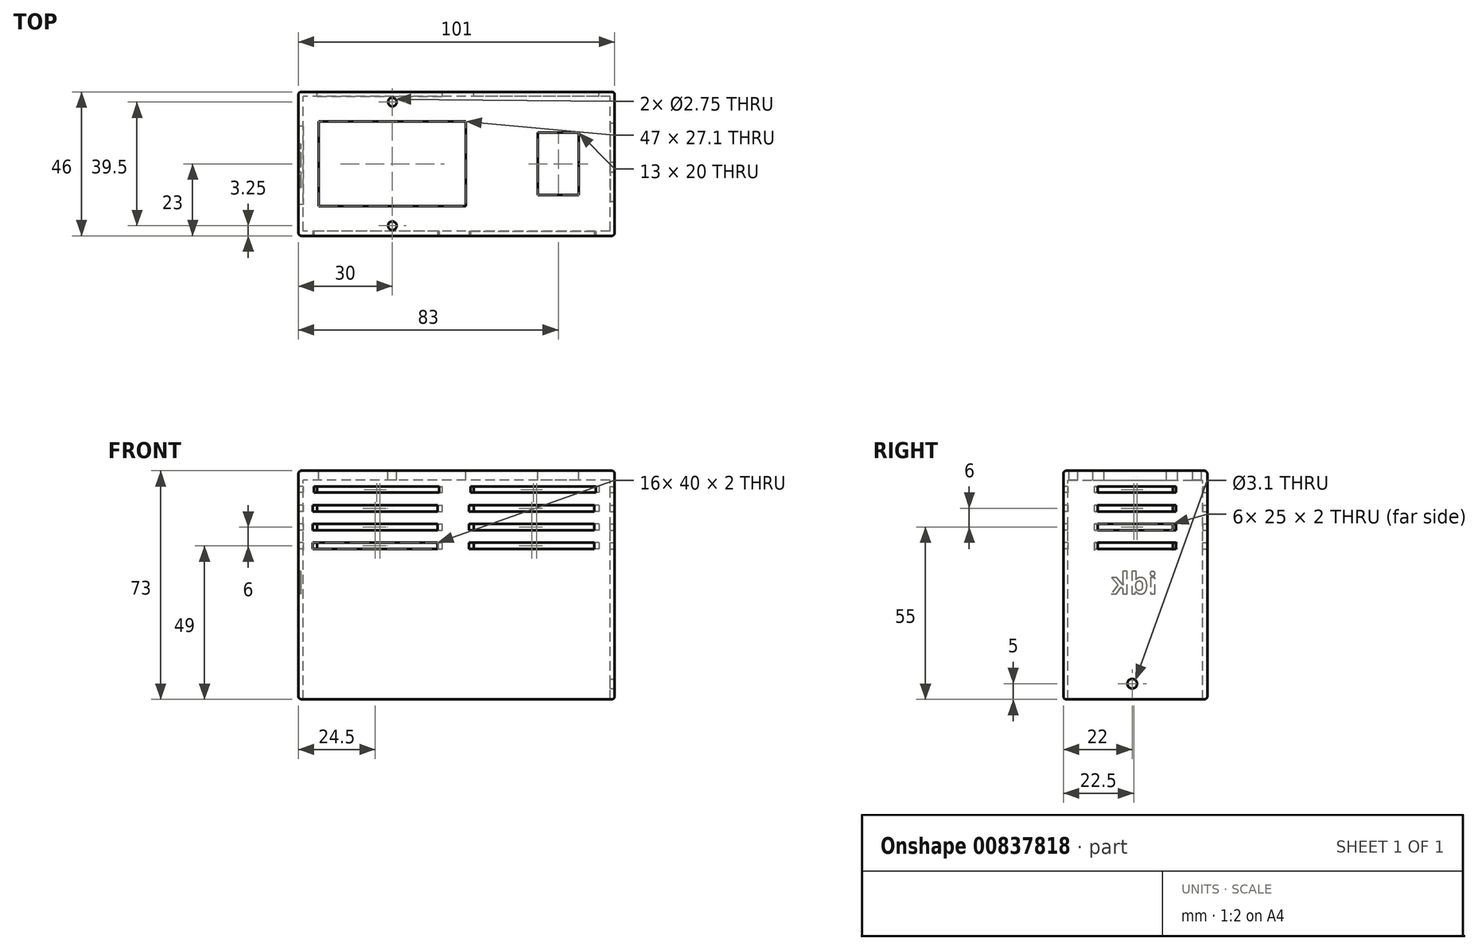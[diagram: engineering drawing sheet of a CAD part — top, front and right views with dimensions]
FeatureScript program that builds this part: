
annotation { "Feature Type Name" : "Feature", "Feature Type Description" : "" }
export const myFeature = defineFeature(function(context is Context, id is Id, definition is map)
    precondition{}
    {
        {
            var Q0;
            Q0=qCreatedBy(makeId("Top.planeOp"),FACE);
            var sketch = newSketch(context, id + "F0", { "sketchPlane" : qUnion([Q0])});
            skLineSegment(sketch, "E0.bottom", {"start": v(49, -21.5) * mm, "end": v(-49, -21.5) * mm});
            skLineSegment(sketch, "E0.top", {"start": v(49, 21.5) * mm, "end": v(-49, 21.5) * mm});
            skLineSegment(sketch, "E0.left", {"start": v(49, -21.5) * mm, "end": v(49, 21.5) * mm});
            skLineSegment(sketch, "E0.right", {"start": v(-49, -21.5) * mm, "end": v(-49, 21.5) * mm});
            skPoint(sketch, "E0.middle", {"position": v(0, 0) * mm});
            skLineSegment(sketch, "E1.bottom", {"start": v(50.5, -23) * mm, "end": v(-50.5, -23) * mm});
            skLineSegment(sketch, "E1.top", {"start": v(50.5, 23) * mm, "end": v(-50.5, 23) * mm});
            skLineSegment(sketch, "E1.left", {"start": v(50.5, -23) * mm, "end": v(50.5, 23) * mm});
            skLineSegment(sketch, "E1.right", {"start": v(-50.5, -23) * mm, "end": v(-50.5, 23) * mm});
            skLineSegment(sketch, "E2.bottom", {"start": v(3, -13.55) * mm, "end": v(-44, -13.55) * mm});
            skLineSegment(sketch, "E2.top", {"start": v(3, 13.55) * mm, "end": v(-44, 13.55) * mm});
            skLineSegment(sketch, "E2.left", {"start": v(3, -13.55) * mm, "end": v(3, 13.55) * mm});
            skLineSegment(sketch, "E2.right", {"start": v(-44, -13.55) * mm, "end": v(-44, 13.55) * mm});
            skPoint(sketch, "E2.middle", {"position": v(-20.5, 0) * mm});
            skLineSegment(sketch, "E3.bottom", {"start": v(39, -10) * mm, "end": v(26, -10) * mm});
            skLineSegment(sketch, "E3.top", {"start": v(39, 10) * mm, "end": v(26, 10) * mm});
            skLineSegment(sketch, "E3.left", {"start": v(39, -10) * mm, "end": v(39, 10) * mm});
            skLineSegment(sketch, "E3.right", {"start": v(26, -10) * mm, "end": v(26, 10) * mm});
            skPoint(sketch, "E3.middle", {"position": v(32.5, 0) * mm});
            skCircle(sketch, "E4", {"center": v(-20.5, -19.75) * mm, "radius": 1.38 * mm});
            skCircle(sketch, "E5", {"center": v(-20.5, 19.75) * mm, "radius": 1.38 * mm});
            skSolve(sketch);
        }
        {
            var Q0;
            Q0=makeQuery(id+"F0.imprint","IMPRINT",FACE,{"disambiguationData":[TD([[makeQuery(id+"F0.imprint","IMPRINT",EDGE,{"derivedFrom":sQuery(id+"F0.wireOp",EDGE,"E0.bottom")}),1.0]])]});
            extrude(context, id + "F1", {"entities" : qUnion([Q0]), "oppositeDirection" : true, "depth" : 73 * mm, "offsetDistance" : 25 * mm});
        }
        {
            var Q0;
            Q0=makeQuery(id+"F0.imprint","IMPRINT",FACE,{"disambiguationData":[TD([[makeQuery(id+"F0.imprint","IMPRINT",EDGE,{"derivedFrom":sQuery(id+"F0.wireOp",EDGE,"E0.bottom")}),-1.0]])]});
            extrude(context, id + "F2", {"entities" : qUnion([Q0]), "operationType" : NewBodyOperationType.ADD, "oppositeDirection" : true, "depth" : 3 * mm, "offsetDistance" : 25 * mm});
        }
        {
            var Q0;
            Q0=qCreatedBy(makeId("Right.planeOp"),FACE);
            cPlane(context, id + "F3", {"entities" : qUnion([Q0]), "cplaneType" : CPlaneType.OFFSET, "offset" : 49 * mm, "width" : 150 * mm, "height" : 150 * mm});
        }
        {
            var Q0;
            Q0=makeQuery(id+"F1.opExtrude","SWEPT_FACE",FACE,{"disambiguationData":[OSD([sQuery(id+"F0.wireOp",EDGE,"E1.left")])]});
            var sketch = newSketch(context, id + "F4", { "sketchPlane" : qUnion([Q0])});
            skCircle(sketch, "E6", {"center": v(-1, -68) * mm, "radius": 1.55 * mm});
            skSolve(sketch);
        }
        {
            var Q0;
            Q0=makeQuery(id+"F4.imprint","IMPRINT",FACE,{"disambiguationData":[TD([[makeQuery(id+"F4.imprint","IMPRINT",EDGE,{"derivedFrom":sQuery(id+"F4.wireOp",EDGE,"E6")}),1.0]])]});
            extrude(context, id + "F5", {"entities" : qUnion([Q0]), "operationType" : NewBodyOperationType.REMOVE, "oppositeDirection" : true, "depth" : 3 * mm, "offsetDistance" : 25 * mm});
        }
        {
            var Q0;
            Q0=makeQuery(id+"F1.opExtrude","CAP_EDGE",EDGE,{"disambiguationData":[OSD([sQuery(id+"F0.wireOp",EDGE,"E1.bottom")])],"isStart":false});
            var Q1;
            Q1=makeQuery(id+"F1.opExtrude","CAP_EDGE",EDGE,{"disambiguationData":[OSD([sQuery(id+"F0.wireOp",EDGE,"E1.left")])],"isStart":false});
            var Q2;
            Q2=makeQuery(id+"F1.opExtrude","CAP_EDGE",EDGE,{"disambiguationData":[OSD([sQuery(id+"F0.wireOp",EDGE,"E1.top")])],"isStart":false});
            var Q3;
            Q3=makeQuery(id+"F1.opExtrude","CAP_EDGE",EDGE,{"disambiguationData":[OSD([sQuery(id+"F0.wireOp",EDGE,"E1.right")])],"isStart":false});
            var Q4;
            Q4=makeQuery(id+"F1.opExtrude","SWEPT_EDGE",EDGE,{"disambiguationData":[OSD([sQuery(id+"F0.wireOp",EDGE,"E1.bottom"),sQuery(id+"F0.wireOp",EDGE,"E1.right")])]});
            var Q5;
            Q5=makeQuery(id+"F1.opExtrude","SWEPT_EDGE",EDGE,{"disambiguationData":[OSD([sQuery(id+"F0.wireOp",EDGE,"E1.top"),sQuery(id+"F0.wireOp",EDGE,"E1.right")])]});
            var Q6;
            Q6=makeQuery(id+"F1.opExtrude","SWEPT_EDGE",EDGE,{"disambiguationData":[OSD([sQuery(id+"F0.wireOp",EDGE,"E1.bottom"),sQuery(id+"F0.wireOp",EDGE,"E1.left")])]});
            var Q7;
            Q7=makeQuery(id+"F1.opExtrude","SWEPT_EDGE",EDGE,{"disambiguationData":[OSD([sQuery(id+"F0.wireOp",EDGE,"E1.top"),sQuery(id+"F0.wireOp",EDGE,"E1.left")])]});
            var Q8;
            Q8=makeQuery(id+"F1.opExtrude","CAP_EDGE",EDGE,{"disambiguationData":[OSD([sQuery(id+"F0.wireOp",EDGE,"E1.bottom")])],"isStart":true});
            var Q9;
            Q9=makeQuery(id+"F1.opExtrude","CAP_EDGE",EDGE,{"disambiguationData":[OSD([sQuery(id+"F0.wireOp",EDGE,"E1.left")])],"isStart":true});
            var Q10;
            Q10=makeQuery(id+"F1.opExtrude","CAP_EDGE",EDGE,{"disambiguationData":[OSD([sQuery(id+"F0.wireOp",EDGE,"E1.top")])],"isStart":true});
            var Q11;
            Q11=makeQuery(id+"F1.opExtrude","CAP_EDGE",EDGE,{"disambiguationData":[OSD([sQuery(id+"F0.wireOp",EDGE,"E1.right")])],"isStart":true});
            var Q12;
            Q12=makeQuery(id+"F5.boolean.opBoolean","COPY",EDGE,{"derivedFrom":makeQuery(id+"F5.opExtrude","CAP_EDGE",EDGE,{"disambiguationData":[OSD([sQuery(id+"F4.wireOp",EDGE,"E6")])],"isStart":true})});
            fillet(context, id + "F6", {"entities" : qUnion([Q0, Q1, Q2, Q3, Q4, Q5, Q6, Q7, Q8, Q9, Q10, Q11, Q12]), "radius" : 1 * mm, "tangentPropagation" : true, "allowEdgeOverflow" : false});
        }
        {
            var Q0;
            Q0=makeQuery(id+"F1.opExtrude","SWEPT_FACE",FACE,{"disambiguationData":[OSD([sQuery(id+"F0.wireOp",EDGE,"E1.bottom")])]});
            var sketch = newSketch(context, id + "F7", { "sketchPlane" : qUnion([Q0])});
            skLineSegment(sketch, "E7.bottom", {"start": v(44.5, -7) * mm, "end": v(4.5, -7) * mm});
            skLineSegment(sketch, "E7.top", {"start": v(44.5, -5) * mm, "end": v(4.5, -5) * mm});
            skLineSegment(sketch, "E7.left", {"start": v(44.5, -7) * mm, "end": v(44.5, -5) * mm});
            skLineSegment(sketch, "E7.right", {"start": v(4.5, -7) * mm, "end": v(4.5, -5) * mm});
            skPoint(sketch, "E7.middle", {"position": v(24.5, -6) * mm});
            skLineSegment(sketch, "E8.bottom", {"start": v(-45.5, -5) * mm, "end": v(-5.5, -5) * mm});
            skLineSegment(sketch, "E8.top", {"start": v(-45.5, -7) * mm, "end": v(-5.5, -7) * mm});
            skLineSegment(sketch, "E8.left", {"start": v(-45.5, -5) * mm, "end": v(-45.5, -7) * mm});
            skLineSegment(sketch, "E8.right", {"start": v(-5.5, -5) * mm, "end": v(-5.5, -7) * mm});
            skPoint(sketch, "E8.middle", {"position": v(-25.5, -6) * mm});
            skLineSegment(sketch, "E9.bottom", {"start": v(44, -13) * mm, "end": v(4, -13) * mm});
            skLineSegment(sketch, "E9.top", {"start": v(44, -11) * mm, "end": v(4, -11) * mm});
            skLineSegment(sketch, "E9.left", {"start": v(44, -13) * mm, "end": v(44, -11) * mm});
            skLineSegment(sketch, "E9.right", {"start": v(4, -13) * mm, "end": v(4, -11) * mm});
            skPoint(sketch, "E9.middle", {"position": v(24, -12) * mm});
            skLineSegment(sketch, "E10.bottom", {"start": v(-46, -11) * mm, "end": v(-6, -11) * mm});
            skLineSegment(sketch, "E10.top", {"start": v(-46, -13) * mm, "end": v(-6, -13) * mm});
            skLineSegment(sketch, "E10.left", {"start": v(-46, -11) * mm, "end": v(-46, -13) * mm});
            skLineSegment(sketch, "E10.right", {"start": v(-6, -11) * mm, "end": v(-6, -13) * mm});
            skPoint(sketch, "E10.middle", {"position": v(-26, -12) * mm});
            skLineSegment(sketch, "E11.bottom", {"start": v(44, -19) * mm, "end": v(4, -19) * mm});
            skLineSegment(sketch, "E11.top", {"start": v(44, -17) * mm, "end": v(4, -17) * mm});
            skLineSegment(sketch, "E11.left", {"start": v(44, -19) * mm, "end": v(44, -17) * mm});
            skLineSegment(sketch, "E11.right", {"start": v(4, -19) * mm, "end": v(4, -17) * mm});
            skPoint(sketch, "E11.middle", {"position": v(24, -18) * mm});
            skLineSegment(sketch, "E12.bottom", {"start": v(-46, -17) * mm, "end": v(-6, -17) * mm});
            skLineSegment(sketch, "E12.top", {"start": v(-46, -19) * mm, "end": v(-6, -19) * mm});
            skLineSegment(sketch, "E12.left", {"start": v(-46, -17) * mm, "end": v(-46, -19) * mm});
            skLineSegment(sketch, "E12.right", {"start": v(-6, -17) * mm, "end": v(-6, -19) * mm});
            skPoint(sketch, "E12.middle", {"position": v(-26, -18) * mm});
            skLineSegment(sketch, "E13.bottom", {"start": v(44, -25) * mm, "end": v(4, -25) * mm});
            skLineSegment(sketch, "E13.top", {"start": v(44, -23) * mm, "end": v(4, -23) * mm});
            skLineSegment(sketch, "E13.left", {"start": v(44, -25) * mm, "end": v(44, -23) * mm});
            skLineSegment(sketch, "E13.right", {"start": v(4, -25) * mm, "end": v(4, -23) * mm});
            skPoint(sketch, "E13.middle", {"position": v(24, -24) * mm});
            skLineSegment(sketch, "E14.bottom", {"start": v(-46, -23) * mm, "end": v(-6, -23) * mm});
            skLineSegment(sketch, "E14.top", {"start": v(-46, -25) * mm, "end": v(-6, -25) * mm});
            skLineSegment(sketch, "E14.left", {"start": v(-46, -23) * mm, "end": v(-46, -25) * mm});
            skLineSegment(sketch, "E14.right", {"start": v(-6, -23) * mm, "end": v(-6, -25) * mm});
            skPoint(sketch, "E14.middle", {"position": v(-26, -24) * mm});
            skSolve(sketch);
        }
        {
            var Q0;
            Q0=makeQuery(id+"F1.opExtrude","SWEPT_FACE",FACE,{"disambiguationData":[OSD([sQuery(id+"F0.wireOp",EDGE,"E1.top")])]});
            var sketch = newSketch(context, id + "F8", { "sketchPlane" : qUnion([Q0])});
            skLineSegment(sketch, "E15.bottom", {"start": v(44.5, -7) * mm, "end": v(4.5, -7) * mm});
            skLineSegment(sketch, "E15.top", {"start": v(44.5, -5) * mm, "end": v(4.5, -5) * mm});
            skLineSegment(sketch, "E15.left", {"start": v(44.5, -7) * mm, "end": v(44.5, -5) * mm});
            skLineSegment(sketch, "E15.right", {"start": v(4.5, -7) * mm, "end": v(4.5, -5) * mm});
            skPoint(sketch, "E15.middle", {"position": v(24.5, -6) * mm});
            skLineSegment(sketch, "E16.bottom", {"start": v(-45.5, -5) * mm, "end": v(-5.5, -5) * mm});
            skLineSegment(sketch, "E16.top", {"start": v(-45.5, -7) * mm, "end": v(-5.5, -7) * mm});
            skLineSegment(sketch, "E16.left", {"start": v(-45.5, -5) * mm, "end": v(-45.5, -7) * mm});
            skLineSegment(sketch, "E16.right", {"start": v(-5.5, -5) * mm, "end": v(-5.5, -7) * mm});
            skPoint(sketch, "E16.middle", {"position": v(-25.5, -6) * mm});
            skLineSegment(sketch, "E17.bottom", {"start": v(44.5, -13) * mm, "end": v(4.5, -13) * mm});
            skLineSegment(sketch, "E17.top", {"start": v(44.5, -11) * mm, "end": v(4.5, -11) * mm});
            skLineSegment(sketch, "E17.left", {"start": v(44.5, -13) * mm, "end": v(44.5, -11) * mm});
            skLineSegment(sketch, "E17.right", {"start": v(4.5, -13) * mm, "end": v(4.5, -11) * mm});
            skPoint(sketch, "E17.middle", {"position": v(24.5, -12) * mm});
            skLineSegment(sketch, "E18.bottom", {"start": v(-45.5, -11) * mm, "end": v(-5.5, -11) * mm});
            skLineSegment(sketch, "E18.top", {"start": v(-45.5, -13) * mm, "end": v(-5.5, -13) * mm});
            skLineSegment(sketch, "E18.left", {"start": v(-45.5, -11) * mm, "end": v(-45.5, -13) * mm});
            skLineSegment(sketch, "E18.right", {"start": v(-5.5, -11) * mm, "end": v(-5.5, -13) * mm});
            skPoint(sketch, "E18.middle", {"position": v(-25.5, -12) * mm});
            skLineSegment(sketch, "E19.bottom", {"start": v(44.5, -19) * mm, "end": v(4.5, -19) * mm});
            skLineSegment(sketch, "E19.top", {"start": v(44.5, -17) * mm, "end": v(4.5, -17) * mm});
            skLineSegment(sketch, "E19.left", {"start": v(44.5, -19) * mm, "end": v(44.5, -17) * mm});
            skLineSegment(sketch, "E19.right", {"start": v(4.5, -19) * mm, "end": v(4.5, -17) * mm});
            skPoint(sketch, "E19.middle", {"position": v(24.5, -18) * mm});
            skLineSegment(sketch, "E20.bottom", {"start": v(-45.5, -17) * mm, "end": v(-5.5, -17) * mm});
            skLineSegment(sketch, "E20.top", {"start": v(-45.5, -19) * mm, "end": v(-5.5, -19) * mm});
            skLineSegment(sketch, "E20.left", {"start": v(-45.5, -17) * mm, "end": v(-45.5, -19) * mm});
            skLineSegment(sketch, "E20.right", {"start": v(-5.5, -17) * mm, "end": v(-5.5, -19) * mm});
            skPoint(sketch, "E20.middle", {"position": v(-25.5, -18) * mm});
            skLineSegment(sketch, "E21.bottom", {"start": v(44.5, -25) * mm, "end": v(4.5, -25) * mm});
            skLineSegment(sketch, "E21.top", {"start": v(44.5, -23) * mm, "end": v(4.5, -23) * mm});
            skLineSegment(sketch, "E21.left", {"start": v(44.5, -25) * mm, "end": v(44.5, -23) * mm});
            skLineSegment(sketch, "E21.right", {"start": v(4.5, -25) * mm, "end": v(4.5, -23) * mm});
            skPoint(sketch, "E21.middle", {"position": v(24.5, -24) * mm});
            skLineSegment(sketch, "E22.bottom", {"start": v(-45.5, -23) * mm, "end": v(-5.5, -23) * mm});
            skLineSegment(sketch, "E22.top", {"start": v(-45.5, -25) * mm, "end": v(-5.5, -25) * mm});
            skLineSegment(sketch, "E22.left", {"start": v(-45.5, -23) * mm, "end": v(-45.5, -25) * mm});
            skLineSegment(sketch, "E22.right", {"start": v(-5.5, -23) * mm, "end": v(-5.5, -25) * mm});
            skPoint(sketch, "E22.middle", {"position": v(-25.5, -24) * mm});
            skSolve(sketch);
        }
        {
            var Q0;
            Q0 = qSketchRegion(id + "F8", true);
            extrude(context, id + "F9", {"entities" : qUnion([Q0]), "operationType" : NewBodyOperationType.REMOVE, "oppositeDirection" : true, "depth" : 3 * mm, "offsetDistance" : 25 * mm});
        }
        {
            var Q0;
            Q0 = qSketchRegion(id + "F7", true);
            extrude(context, id + "F10", {"entities" : qUnion([Q0]), "operationType" : NewBodyOperationType.REMOVE, "oppositeDirection" : true, "depth" : 3 * mm, "offsetDistance" : 25 * mm});
        }
        {
            var Q0;
            Q0=makeQuery(id+"F1.opExtrude","SWEPT_FACE",FACE,{"disambiguationData":[OSD([sQuery(id+"F0.wireOp",EDGE,"E1.left")])]});
            var sketch = newSketch(context, id + "F11", { "sketchPlane" : qUnion([Q0])});
            skLineSegment(sketch, "E23.bottom", {"start": v(13, -7) * mm, "end": v(-12, -7) * mm});
            skLineSegment(sketch, "E23.top", {"start": v(13, -5) * mm, "end": v(-12, -5) * mm});
            skLineSegment(sketch, "E23.left", {"start": v(13, -7) * mm, "end": v(13, -5) * mm});
            skLineSegment(sketch, "E23.right", {"start": v(-12, -7) * mm, "end": v(-12, -5) * mm});
            skPoint(sketch, "E23.middle", {"position": v(0.5, -6) * mm});
            skLineSegment(sketch, "E24.bottom", {"start": v(13, -13) * mm, "end": v(-12, -13) * mm});
            skLineSegment(sketch, "E24.top", {"start": v(13, -11) * mm, "end": v(-12, -11) * mm});
            skLineSegment(sketch, "E24.left", {"start": v(13, -13) * mm, "end": v(13, -11) * mm});
            skLineSegment(sketch, "E24.right", {"start": v(-12, -13) * mm, "end": v(-12, -11) * mm});
            skPoint(sketch, "E24.middle", {"position": v(0.5, -12) * mm});
            skLineSegment(sketch, "E25.bottom", {"start": v(13, -19) * mm, "end": v(-12, -19) * mm});
            skLineSegment(sketch, "E25.top", {"start": v(13, -17) * mm, "end": v(-12, -17) * mm});
            skLineSegment(sketch, "E25.left", {"start": v(13, -19) * mm, "end": v(13, -17) * mm});
            skLineSegment(sketch, "E25.right", {"start": v(-12, -19) * mm, "end": v(-12, -17) * mm});
            skPoint(sketch, "E25.middle", {"position": v(0.5, -18) * mm});
            skLineSegment(sketch, "E26.bottom", {"start": v(13, -25) * mm, "end": v(-12, -25) * mm});
            skLineSegment(sketch, "E26.top", {"start": v(13, -23) * mm, "end": v(-12, -23) * mm});
            skLineSegment(sketch, "E26.left", {"start": v(13, -25) * mm, "end": v(13, -23) * mm});
            skLineSegment(sketch, "E26.right", {"start": v(-12, -25) * mm, "end": v(-12, -23) * mm});
            skPoint(sketch, "E26.middle", {"position": v(0.5, -24) * mm});
            skSolve(sketch);
        }
        {
            var Q0;
            Q0 = qSketchRegion(id + "F11", true);
            extrude(context, id + "F12", {"entities" : qUnion([Q0]), "operationType" : NewBodyOperationType.REMOVE, "oppositeDirection" : true, "depth" : 3 * mm, "offsetDistance" : 25 * mm});
        }
        {
            var Q0;
            Q0=makeQuery(id+"F1.opExtrude","SWEPT_FACE",FACE,{"disambiguationData":[OSD([sQuery(id+"F0.wireOp",EDGE,"E1.right")])]});
            var sketch = newSketch(context, id + "F13", { "sketchPlane" : qUnion([Q0])});
            skLineSegment(sketch, "E27.bottom", {"start": v(13, -7) * mm, "end": v(-12, -7) * mm});
            skLineSegment(sketch, "E27.top", {"start": v(13, -5) * mm, "end": v(-12, -5) * mm});
            skLineSegment(sketch, "E27.left", {"start": v(13, -7) * mm, "end": v(13, -5) * mm});
            skLineSegment(sketch, "E27.right", {"start": v(-12, -7) * mm, "end": v(-12, -5) * mm});
            skPoint(sketch, "E27.middle", {"position": v(0.5, -6) * mm});
            skLineSegment(sketch, "E28.bottom", {"start": v(13, -13) * mm, "end": v(-12, -13) * mm});
            skLineSegment(sketch, "E28.top", {"start": v(13, -11) * mm, "end": v(-12, -11) * mm});
            skLineSegment(sketch, "E28.left", {"start": v(13, -13) * mm, "end": v(13, -11) * mm});
            skLineSegment(sketch, "E28.right", {"start": v(-12, -13) * mm, "end": v(-12, -11) * mm});
            skPoint(sketch, "E28.middle", {"position": v(0.5, -12) * mm});
            skLineSegment(sketch, "E29.bottom", {"start": v(13, -19) * mm, "end": v(-12, -19) * mm});
            skLineSegment(sketch, "E29.top", {"start": v(13, -17) * mm, "end": v(-12, -17) * mm});
            skLineSegment(sketch, "E29.left", {"start": v(13, -19) * mm, "end": v(13, -17) * mm});
            skLineSegment(sketch, "E29.right", {"start": v(-12, -19) * mm, "end": v(-12, -17) * mm});
            skPoint(sketch, "E29.middle", {"position": v(0.5, -18) * mm});
            skLineSegment(sketch, "E30.bottom", {"start": v(13, -25) * mm, "end": v(-12, -25) * mm});
            skLineSegment(sketch, "E30.top", {"start": v(13, -23) * mm, "end": v(-12, -23) * mm});
            skLineSegment(sketch, "E30.left", {"start": v(13, -25) * mm, "end": v(13, -23) * mm});
            skLineSegment(sketch, "E30.right", {"start": v(-12, -25) * mm, "end": v(-12, -23) * mm});
            skPoint(sketch, "E30.middle", {"position": v(0.5, -24) * mm});
            skSolve(sketch);
        }
        {
            var Q0;
            Q0 = qSketchRegion(id + "F13", true);
            extrude(context, id + "F14", {"entities" : qUnion([Q0]), "operationType" : NewBodyOperationType.REMOVE, "oppositeDirection" : true, "depth" : 3 * mm, "offsetDistance" : 25 * mm});
        }
        {
            var Q0;
            Q0=makeQuery(id+"F10.boolean.opBoolean","COPY",EDGE,{"derivedFrom":makeQuery(id+"F10.opExtrude","CAP_EDGE",EDGE,{"disambiguationData":[OSD([sQuery(id+"F7.wireOp",EDGE,"E13.left")])],"isStart":true})});
            var Q1;
            Q1=makeQuery(id+"F10.boolean.opBoolean","COPY",EDGE,{"derivedFrom":makeQuery(id+"F10.opExtrude","CAP_EDGE",EDGE,{"disambiguationData":[OSD([sQuery(id+"F7.wireOp",EDGE,"E13.bottom")])],"isStart":true})});
            var Q2;
            Q2=makeQuery(id+"F10.boolean.opBoolean","COPY",EDGE,{"derivedFrom":makeQuery(id+"F10.opExtrude","CAP_EDGE",EDGE,{"disambiguationData":[OSD([sQuery(id+"F7.wireOp",EDGE,"E13.top")])],"isStart":true})});
            var Q3;
            Q3=makeQuery(id+"F10.boolean.opBoolean","COPY",EDGE,{"derivedFrom":makeQuery(id+"F10.opExtrude","CAP_EDGE",EDGE,{"disambiguationData":[OSD([sQuery(id+"F7.wireOp",EDGE,"E13.right")])],"isStart":true})});
            var Q4;
            Q4=makeQuery(id+"F10.boolean.opBoolean","COPY",EDGE,{"derivedFrom":makeQuery(id+"F10.opExtrude","CAP_EDGE",EDGE,{"disambiguationData":[OSD([sQuery(id+"F7.wireOp",EDGE,"E11.bottom")])],"isStart":true})});
            var Q5;
            Q5=makeQuery(id+"F10.boolean.opBoolean","COPY",EDGE,{"derivedFrom":makeQuery(id+"F10.opExtrude","CAP_EDGE",EDGE,{"disambiguationData":[OSD([sQuery(id+"F7.wireOp",EDGE,"E11.left")])],"isStart":true})});
            var Q6;
            Q6=makeQuery(id+"F10.boolean.opBoolean","COPY",EDGE,{"derivedFrom":makeQuery(id+"F10.opExtrude","CAP_EDGE",EDGE,{"disambiguationData":[OSD([sQuery(id+"F7.wireOp",EDGE,"E11.top")])],"isStart":true})});
            var Q7;
            Q7=makeQuery(id+"F10.boolean.opBoolean","COPY",EDGE,{"derivedFrom":makeQuery(id+"F10.opExtrude","CAP_EDGE",EDGE,{"disambiguationData":[OSD([sQuery(id+"F7.wireOp",EDGE,"E11.right")])],"isStart":true})});
            var Q8;
            Q8=makeQuery(id+"F10.boolean.opBoolean","COPY",EDGE,{"derivedFrom":makeQuery(id+"F10.opExtrude","CAP_EDGE",EDGE,{"disambiguationData":[OSD([sQuery(id+"F7.wireOp",EDGE,"E9.right")])],"isStart":true})});
            var Q9;
            Q9=makeQuery(id+"F10.boolean.opBoolean","COPY",EDGE,{"derivedFrom":makeQuery(id+"F10.opExtrude","CAP_EDGE",EDGE,{"disambiguationData":[OSD([sQuery(id+"F7.wireOp",EDGE,"E9.bottom")])],"isStart":true})});
            var Q10;
            Q10=makeQuery(id+"F10.boolean.opBoolean","COPY",EDGE,{"derivedFrom":makeQuery(id+"F10.opExtrude","CAP_EDGE",EDGE,{"disambiguationData":[OSD([sQuery(id+"F7.wireOp",EDGE,"E9.left")])],"isStart":true})});
            var Q11;
            Q11=makeQuery(id+"F10.boolean.opBoolean","COPY",EDGE,{"derivedFrom":makeQuery(id+"F10.opExtrude","CAP_EDGE",EDGE,{"disambiguationData":[OSD([sQuery(id+"F7.wireOp",EDGE,"E9.top")])],"isStart":true})});
            var Q12;
            Q12=makeQuery(id+"F10.boolean.opBoolean","COPY",EDGE,{"derivedFrom":makeQuery(id+"F10.opExtrude","CAP_EDGE",EDGE,{"disambiguationData":[OSD([sQuery(id+"F7.wireOp",EDGE,"E7.bottom")])],"isStart":true})});
            var Q13;
            Q13=makeQuery(id+"F10.boolean.opBoolean","COPY",EDGE,{"derivedFrom":makeQuery(id+"F10.opExtrude","CAP_EDGE",EDGE,{"disambiguationData":[OSD([sQuery(id+"F7.wireOp",EDGE,"E7.left")])],"isStart":true})});
            var Q14;
            Q14=makeQuery(id+"F10.boolean.opBoolean","COPY",EDGE,{"derivedFrom":makeQuery(id+"F10.opExtrude","CAP_EDGE",EDGE,{"disambiguationData":[OSD([sQuery(id+"F7.wireOp",EDGE,"E7.top")])],"isStart":true})});
            var Q15;
            Q15=makeQuery(id+"F10.boolean.opBoolean","COPY",EDGE,{"derivedFrom":makeQuery(id+"F10.opExtrude","CAP_EDGE",EDGE,{"disambiguationData":[OSD([sQuery(id+"F7.wireOp",EDGE,"E7.right")])],"isStart":true})});
            var Q16;
            Q16=makeQuery(id+"F10.boolean.opBoolean","COPY",EDGE,{"derivedFrom":makeQuery(id+"F10.opExtrude","CAP_EDGE",EDGE,{"disambiguationData":[OSD([sQuery(id+"F7.wireOp",EDGE,"E14.right")])],"isStart":true})});
            var Q17;
            Q17=makeQuery(id+"F10.boolean.opBoolean","COPY",EDGE,{"derivedFrom":makeQuery(id+"F10.opExtrude","CAP_EDGE",EDGE,{"disambiguationData":[OSD([sQuery(id+"F7.wireOp",EDGE,"E14.top")])],"isStart":true})});
            var Q18;
            Q18=makeQuery(id+"F10.boolean.opBoolean","COPY",EDGE,{"derivedFrom":makeQuery(id+"F10.opExtrude","CAP_EDGE",EDGE,{"disambiguationData":[OSD([sQuery(id+"F7.wireOp",EDGE,"E14.left")])],"isStart":true})});
            var Q19;
            Q19=makeQuery(id+"F10.boolean.opBoolean","COPY",EDGE,{"derivedFrom":makeQuery(id+"F10.opExtrude","CAP_EDGE",EDGE,{"disambiguationData":[OSD([sQuery(id+"F7.wireOp",EDGE,"E14.bottom")])],"isStart":true})});
            var Q20;
            Q20=makeQuery(id+"F10.boolean.opBoolean","COPY",EDGE,{"derivedFrom":makeQuery(id+"F10.opExtrude","CAP_EDGE",EDGE,{"disambiguationData":[OSD([sQuery(id+"F7.wireOp",EDGE,"E12.top")])],"isStart":true})});
            var Q21;
            Q21=makeQuery(id+"F10.boolean.opBoolean","COPY",EDGE,{"derivedFrom":makeQuery(id+"F10.opExtrude","CAP_EDGE",EDGE,{"disambiguationData":[OSD([sQuery(id+"F7.wireOp",EDGE,"E12.right")])],"isStart":true})});
            var Q22;
            Q22=makeQuery(id+"F10.boolean.opBoolean","COPY",EDGE,{"derivedFrom":makeQuery(id+"F10.opExtrude","CAP_EDGE",EDGE,{"disambiguationData":[OSD([sQuery(id+"F7.wireOp",EDGE,"E12.bottom")])],"isStart":true})});
            var Q23;
            Q23=makeQuery(id+"F10.boolean.opBoolean","COPY",EDGE,{"derivedFrom":makeQuery(id+"F10.opExtrude","CAP_EDGE",EDGE,{"disambiguationData":[OSD([sQuery(id+"F7.wireOp",EDGE,"E12.left")])],"isStart":true})});
            var Q24;
            Q24=makeQuery(id+"F10.boolean.opBoolean","COPY",EDGE,{"derivedFrom":makeQuery(id+"F10.opExtrude","CAP_EDGE",EDGE,{"disambiguationData":[OSD([sQuery(id+"F7.wireOp",EDGE,"E10.left")])],"isStart":true})});
            var Q25;
            Q25=makeQuery(id+"F10.boolean.opBoolean","COPY",EDGE,{"derivedFrom":makeQuery(id+"F10.opExtrude","CAP_EDGE",EDGE,{"disambiguationData":[OSD([sQuery(id+"F7.wireOp",EDGE,"E10.top")])],"isStart":true})});
            var Q26;
            Q26=makeQuery(id+"F10.boolean.opBoolean","COPY",EDGE,{"derivedFrom":makeQuery(id+"F10.opExtrude","CAP_EDGE",EDGE,{"disambiguationData":[OSD([sQuery(id+"F7.wireOp",EDGE,"E10.right")])],"isStart":true})});
            var Q27;
            Q27=makeQuery(id+"F10.boolean.opBoolean","COPY",EDGE,{"derivedFrom":makeQuery(id+"F10.opExtrude","CAP_EDGE",EDGE,{"disambiguationData":[OSD([sQuery(id+"F7.wireOp",EDGE,"E10.bottom")])],"isStart":true})});
            var Q28;
            Q28=makeQuery(id+"F10.boolean.opBoolean","COPY",EDGE,{"derivedFrom":makeQuery(id+"F10.opExtrude","CAP_EDGE",EDGE,{"disambiguationData":[OSD([sQuery(id+"F7.wireOp",EDGE,"E8.top")])],"isStart":true})});
            var Q29;
            Q29=makeQuery(id+"F10.boolean.opBoolean","COPY",EDGE,{"derivedFrom":makeQuery(id+"F10.opExtrude","CAP_EDGE",EDGE,{"disambiguationData":[OSD([sQuery(id+"F7.wireOp",EDGE,"E8.right")])],"isStart":true})});
            var Q30;
            Q30=makeQuery(id+"F10.boolean.opBoolean","COPY",EDGE,{"derivedFrom":makeQuery(id+"F10.opExtrude","CAP_EDGE",EDGE,{"disambiguationData":[OSD([sQuery(id+"F7.wireOp",EDGE,"E8.bottom")])],"isStart":true})});
            var Q31;
            Q31=makeQuery(id+"F10.boolean.opBoolean","COPY",EDGE,{"derivedFrom":makeQuery(id+"F10.opExtrude","CAP_EDGE",EDGE,{"disambiguationData":[OSD([sQuery(id+"F7.wireOp",EDGE,"E8.left")])],"isStart":true})});
            var Q32;
            Q32=makeQuery(id+"F12.boolean.opBoolean","COPY",EDGE,{"derivedFrom":makeQuery(id+"F12.opExtrude","CAP_EDGE",EDGE,{"disambiguationData":[OSD([sQuery(id+"F11.wireOp",EDGE,"E26.bottom")])],"isStart":true})});
            var Q33;
            Q33=makeQuery(id+"F12.boolean.opBoolean","INTERSECT",EDGE,{"derivedFrom":[makeQuery(id+"F1.opExtrude","SWEPT_FACE",FACE,{"disambiguationData":[OSD([sQuery(id+"F0.wireOp",EDGE,"E0.left")])]}),makeQuery(id+"F12.opExtrude","SWEPT_FACE",FACE,{"disambiguationData":[OSD([sQuery(id+"F11.wireOp",EDGE,"E26.left")])]})]});
            var Q34;
            Q34=makeQuery(id+"F12.boolean.opBoolean","COPY",EDGE,{"derivedFrom":makeQuery(id+"F12.opExtrude","CAP_EDGE",EDGE,{"disambiguationData":[OSD([sQuery(id+"F11.wireOp",EDGE,"E26.top")])],"isStart":true})});
            var Q35;
            Q35=makeQuery(id+"F12.boolean.opBoolean","COPY",EDGE,{"derivedFrom":makeQuery(id+"F12.opExtrude","CAP_EDGE",EDGE,{"disambiguationData":[OSD([sQuery(id+"F11.wireOp",EDGE,"E26.right")])],"isStart":true})});
            var Q36;
            Q36=makeQuery(id+"F12.boolean.opBoolean","COPY",EDGE,{"derivedFrom":makeQuery(id+"F12.opExtrude","CAP_EDGE",EDGE,{"disambiguationData":[OSD([sQuery(id+"F11.wireOp",EDGE,"E25.right")])],"isStart":true})});
            var Q37;
            Q37=makeQuery(id+"F12.boolean.opBoolean","COPY",EDGE,{"derivedFrom":makeQuery(id+"F12.opExtrude","CAP_EDGE",EDGE,{"disambiguationData":[OSD([sQuery(id+"F11.wireOp",EDGE,"E25.bottom")])],"isStart":true})});
            var Q38;
            Q38=makeQuery(id+"F12.boolean.opBoolean","COPY",EDGE,{"derivedFrom":makeQuery(id+"F12.opExtrude","CAP_EDGE",EDGE,{"disambiguationData":[OSD([sQuery(id+"F11.wireOp",EDGE,"E25.left")])],"isStart":true})});
            var Q39;
            Q39=makeQuery(id+"F12.boolean.opBoolean","COPY",EDGE,{"derivedFrom":makeQuery(id+"F12.opExtrude","CAP_EDGE",EDGE,{"disambiguationData":[OSD([sQuery(id+"F11.wireOp",EDGE,"E25.top")])],"isStart":true})});
            var Q40;
            Q40=makeQuery(id+"F12.boolean.opBoolean","COPY",EDGE,{"derivedFrom":makeQuery(id+"F12.opExtrude","CAP_EDGE",EDGE,{"disambiguationData":[OSD([sQuery(id+"F11.wireOp",EDGE,"E24.left")])],"isStart":true})});
            var Q41;
            Q41=makeQuery(id+"F12.boolean.opBoolean","COPY",EDGE,{"derivedFrom":makeQuery(id+"F12.opExtrude","CAP_EDGE",EDGE,{"disambiguationData":[OSD([sQuery(id+"F11.wireOp",EDGE,"E24.bottom")])],"isStart":true})});
            var Q42;
            Q42=makeQuery(id+"F12.boolean.opBoolean","COPY",EDGE,{"derivedFrom":makeQuery(id+"F12.opExtrude","CAP_EDGE",EDGE,{"disambiguationData":[OSD([sQuery(id+"F11.wireOp",EDGE,"E24.top")])],"isStart":true})});
            var Q43;
            Q43=makeQuery(id+"F12.boolean.opBoolean","COPY",EDGE,{"derivedFrom":makeQuery(id+"F12.opExtrude","CAP_EDGE",EDGE,{"disambiguationData":[OSD([sQuery(id+"F11.wireOp",EDGE,"E24.right")])],"isStart":true})});
            var Q44;
            Q44=makeQuery(id+"F12.boolean.opBoolean","COPY",EDGE,{"derivedFrom":makeQuery(id+"F12.opExtrude","CAP_EDGE",EDGE,{"disambiguationData":[OSD([sQuery(id+"F11.wireOp",EDGE,"E23.right")])],"isStart":true})});
            var Q45;
            Q45=makeQuery(id+"F12.boolean.opBoolean","COPY",EDGE,{"derivedFrom":makeQuery(id+"F12.opExtrude","CAP_EDGE",EDGE,{"disambiguationData":[OSD([sQuery(id+"F11.wireOp",EDGE,"E23.bottom")])],"isStart":true})});
            var Q46;
            Q46=makeQuery(id+"F12.boolean.opBoolean","COPY",EDGE,{"derivedFrom":makeQuery(id+"F12.opExtrude","CAP_EDGE",EDGE,{"disambiguationData":[OSD([sQuery(id+"F11.wireOp",EDGE,"E23.left")])],"isStart":true})});
            var Q47;
            Q47=makeQuery(id+"F12.boolean.opBoolean","COPY",EDGE,{"derivedFrom":makeQuery(id+"F12.opExtrude","CAP_EDGE",EDGE,{"disambiguationData":[OSD([sQuery(id+"F11.wireOp",EDGE,"E23.top")])],"isStart":true})});
            var Q48;
            Q48=makeQuery(id+"F12.boolean.opBoolean","COPY",EDGE,{"derivedFrom":makeQuery(id+"F12.opExtrude","CAP_EDGE",EDGE,{"disambiguationData":[OSD([sQuery(id+"F11.wireOp",EDGE,"E26.left")])],"isStart":true})});
            var Q49;
            Q49=makeQuery(id+"F9.boolean.opBoolean","COPY",EDGE,{"derivedFrom":makeQuery(id+"F9.opExtrude","CAP_EDGE",EDGE,{"disambiguationData":[OSD([sQuery(id+"F8.wireOp",EDGE,"E22.top")])],"isStart":true})});
            var Q50;
            Q50=makeQuery(id+"F9.boolean.opBoolean","COPY",EDGE,{"derivedFrom":makeQuery(id+"F9.opExtrude","CAP_EDGE",EDGE,{"disambiguationData":[OSD([sQuery(id+"F8.wireOp",EDGE,"E22.right")])],"isStart":true})});
            var Q51;
            Q51=makeQuery(id+"F9.boolean.opBoolean","COPY",EDGE,{"derivedFrom":makeQuery(id+"F9.opExtrude","CAP_EDGE",EDGE,{"disambiguationData":[OSD([sQuery(id+"F8.wireOp",EDGE,"E22.left")])],"isStart":true})});
            var Q52;
            Q52=makeQuery(id+"F9.boolean.opBoolean","COPY",EDGE,{"derivedFrom":makeQuery(id+"F9.opExtrude","CAP_EDGE",EDGE,{"disambiguationData":[OSD([sQuery(id+"F8.wireOp",EDGE,"E22.bottom")])],"isStart":true})});
            var Q53;
            Q53=makeQuery(id+"F9.boolean.opBoolean","COPY",EDGE,{"derivedFrom":makeQuery(id+"F9.opExtrude","CAP_EDGE",EDGE,{"disambiguationData":[OSD([sQuery(id+"F8.wireOp",EDGE,"E20.top")])],"isStart":true})});
            var Q54;
            Q54=makeQuery(id+"F9.boolean.opBoolean","COPY",EDGE,{"derivedFrom":makeQuery(id+"F9.opExtrude","CAP_EDGE",EDGE,{"disambiguationData":[OSD([sQuery(id+"F8.wireOp",EDGE,"E20.left")])],"isStart":true})});
            var Q55;
            Q55=makeQuery(id+"F9.boolean.opBoolean","COPY",EDGE,{"derivedFrom":makeQuery(id+"F9.opExtrude","CAP_EDGE",EDGE,{"disambiguationData":[OSD([sQuery(id+"F8.wireOp",EDGE,"E20.bottom")])],"isStart":true})});
            var Q56;
            Q56=makeQuery(id+"F9.boolean.opBoolean","COPY",EDGE,{"derivedFrom":makeQuery(id+"F9.opExtrude","CAP_EDGE",EDGE,{"disambiguationData":[OSD([sQuery(id+"F8.wireOp",EDGE,"E20.right")])],"isStart":true})});
            var Q57;
            Q57=makeQuery(id+"F9.boolean.opBoolean","COPY",EDGE,{"derivedFrom":makeQuery(id+"F9.opExtrude","CAP_EDGE",EDGE,{"disambiguationData":[OSD([sQuery(id+"F8.wireOp",EDGE,"E18.right")])],"isStart":true})});
            var Q58;
            Q58=makeQuery(id+"F9.boolean.opBoolean","COPY",EDGE,{"derivedFrom":makeQuery(id+"F9.opExtrude","CAP_EDGE",EDGE,{"disambiguationData":[OSD([sQuery(id+"F8.wireOp",EDGE,"E18.top")])],"isStart":true})});
            var Q59;
            Q59=makeQuery(id+"F9.boolean.opBoolean","COPY",EDGE,{"derivedFrom":makeQuery(id+"F9.opExtrude","CAP_EDGE",EDGE,{"disambiguationData":[OSD([sQuery(id+"F8.wireOp",EDGE,"E18.bottom")])],"isStart":true})});
            var Q60;
            Q60=makeQuery(id+"F9.boolean.opBoolean","COPY",EDGE,{"derivedFrom":makeQuery(id+"F9.opExtrude","CAP_EDGE",EDGE,{"disambiguationData":[OSD([sQuery(id+"F8.wireOp",EDGE,"E18.left")])],"isStart":true})});
            var Q61;
            Q61=makeQuery(id+"F9.boolean.opBoolean","COPY",EDGE,{"derivedFrom":makeQuery(id+"F9.opExtrude","CAP_EDGE",EDGE,{"disambiguationData":[OSD([sQuery(id+"F8.wireOp",EDGE,"E16.left")])],"isStart":true})});
            var Q62;
            Q62=makeQuery(id+"F9.boolean.opBoolean","COPY",EDGE,{"derivedFrom":makeQuery(id+"F9.opExtrude","CAP_EDGE",EDGE,{"disambiguationData":[OSD([sQuery(id+"F8.wireOp",EDGE,"E16.top")])],"isStart":true})});
            var Q63;
            Q63=makeQuery(id+"F9.boolean.opBoolean","COPY",EDGE,{"derivedFrom":makeQuery(id+"F9.opExtrude","CAP_EDGE",EDGE,{"disambiguationData":[OSD([sQuery(id+"F8.wireOp",EDGE,"E16.bottom")])],"isStart":true})});
            var Q64;
            Q64=makeQuery(id+"F9.boolean.opBoolean","COPY",EDGE,{"derivedFrom":makeQuery(id+"F9.opExtrude","CAP_EDGE",EDGE,{"disambiguationData":[OSD([sQuery(id+"F8.wireOp",EDGE,"E16.right")])],"isStart":true})});
            var Q65;
            Q65=makeQuery(id+"F9.boolean.opBoolean","COPY",EDGE,{"derivedFrom":makeQuery(id+"F9.opExtrude","CAP_EDGE",EDGE,{"disambiguationData":[OSD([sQuery(id+"F8.wireOp",EDGE,"E21.right")])],"isStart":true})});
            var Q66;
            Q66=makeQuery(id+"F9.boolean.opBoolean","COPY",EDGE,{"derivedFrom":makeQuery(id+"F9.opExtrude","CAP_EDGE",EDGE,{"disambiguationData":[OSD([sQuery(id+"F8.wireOp",EDGE,"E21.bottom")])],"isStart":true})});
            var Q67;
            Q67=makeQuery(id+"F9.boolean.opBoolean","COPY",EDGE,{"derivedFrom":makeQuery(id+"F9.opExtrude","CAP_EDGE",EDGE,{"disambiguationData":[OSD([sQuery(id+"F8.wireOp",EDGE,"E21.left")])],"isStart":true})});
            var Q68;
            Q68=makeQuery(id+"F9.boolean.opBoolean","COPY",EDGE,{"derivedFrom":makeQuery(id+"F9.opExtrude","CAP_EDGE",EDGE,{"disambiguationData":[OSD([sQuery(id+"F8.wireOp",EDGE,"E21.top")])],"isStart":true})});
            var Q69;
            Q69=makeQuery(id+"F9.boolean.opBoolean","COPY",EDGE,{"derivedFrom":makeQuery(id+"F9.opExtrude","CAP_EDGE",EDGE,{"disambiguationData":[OSD([sQuery(id+"F8.wireOp",EDGE,"E19.bottom")])],"isStart":true})});
            var Q70;
            Q70=makeQuery(id+"F9.boolean.opBoolean","COPY",EDGE,{"derivedFrom":makeQuery(id+"F9.opExtrude","CAP_EDGE",EDGE,{"disambiguationData":[OSD([sQuery(id+"F8.wireOp",EDGE,"E19.left")])],"isStart":true})});
            var Q71;
            Q71=makeQuery(id+"F9.boolean.opBoolean","COPY",EDGE,{"derivedFrom":makeQuery(id+"F9.opExtrude","CAP_EDGE",EDGE,{"disambiguationData":[OSD([sQuery(id+"F8.wireOp",EDGE,"E19.top")])],"isStart":true})});
            var Q72;
            Q72=makeQuery(id+"F9.boolean.opBoolean","COPY",EDGE,{"derivedFrom":makeQuery(id+"F9.opExtrude","CAP_EDGE",EDGE,{"disambiguationData":[OSD([sQuery(id+"F8.wireOp",EDGE,"E19.right")])],"isStart":true})});
            var Q73;
            Q73=makeQuery(id+"F9.boolean.opBoolean","COPY",EDGE,{"derivedFrom":makeQuery(id+"F9.opExtrude","CAP_EDGE",EDGE,{"disambiguationData":[OSD([sQuery(id+"F8.wireOp",EDGE,"E17.right")])],"isStart":true})});
            var Q74;
            Q74=makeQuery(id+"F9.boolean.opBoolean","COPY",EDGE,{"derivedFrom":makeQuery(id+"F9.opExtrude","CAP_EDGE",EDGE,{"disambiguationData":[OSD([sQuery(id+"F8.wireOp",EDGE,"E17.bottom")])],"isStart":true})});
            var Q75;
            Q75=makeQuery(id+"F9.boolean.opBoolean","COPY",EDGE,{"derivedFrom":makeQuery(id+"F9.opExtrude","CAP_EDGE",EDGE,{"disambiguationData":[OSD([sQuery(id+"F8.wireOp",EDGE,"E17.top")])],"isStart":true})});
            var Q76;
            Q76=makeQuery(id+"F9.boolean.opBoolean","COPY",EDGE,{"derivedFrom":makeQuery(id+"F9.opExtrude","CAP_EDGE",EDGE,{"disambiguationData":[OSD([sQuery(id+"F8.wireOp",EDGE,"E17.left")])],"isStart":true})});
            var Q77;
            Q77=makeQuery(id+"F9.boolean.opBoolean","COPY",EDGE,{"derivedFrom":makeQuery(id+"F9.opExtrude","CAP_EDGE",EDGE,{"disambiguationData":[OSD([sQuery(id+"F8.wireOp",EDGE,"E15.left")])],"isStart":true})});
            var Q78;
            Q78=makeQuery(id+"F9.boolean.opBoolean","COPY",EDGE,{"derivedFrom":makeQuery(id+"F9.opExtrude","CAP_EDGE",EDGE,{"disambiguationData":[OSD([sQuery(id+"F8.wireOp",EDGE,"E15.bottom")])],"isStart":true})});
            var Q79;
            Q79=makeQuery(id+"F9.boolean.opBoolean","COPY",EDGE,{"derivedFrom":makeQuery(id+"F9.opExtrude","CAP_EDGE",EDGE,{"disambiguationData":[OSD([sQuery(id+"F8.wireOp",EDGE,"E15.top")])],"isStart":true})});
            var Q80;
            Q80=makeQuery(id+"F9.boolean.opBoolean","COPY",EDGE,{"derivedFrom":makeQuery(id+"F9.opExtrude","CAP_EDGE",EDGE,{"disambiguationData":[OSD([sQuery(id+"F8.wireOp",EDGE,"E15.right")])],"isStart":true})});
            var Q81;
            Q81=makeQuery(id+"F14.boolean.opBoolean","COPY",EDGE,{"derivedFrom":makeQuery(id+"F14.opExtrude","CAP_EDGE",EDGE,{"disambiguationData":[OSD([sQuery(id+"F13.wireOp",EDGE,"E27.top")])],"isStart":true})});
            var Q82;
            Q82=makeQuery(id+"F14.boolean.opBoolean","COPY",EDGE,{"derivedFrom":makeQuery(id+"F14.opExtrude","CAP_EDGE",EDGE,{"disambiguationData":[OSD([sQuery(id+"F13.wireOp",EDGE,"E27.bottom")])],"isStart":true})});
            var Q83;
            Q83=makeQuery(id+"F14.boolean.opBoolean","COPY",EDGE,{"derivedFrom":makeQuery(id+"F14.opExtrude","CAP_EDGE",EDGE,{"disambiguationData":[OSD([sQuery(id+"F13.wireOp",EDGE,"E27.right")])],"isStart":true})});
            var Q84;
            Q84=makeQuery(id+"F14.boolean.opBoolean","COPY",EDGE,{"derivedFrom":makeQuery(id+"F14.opExtrude","CAP_EDGE",EDGE,{"disambiguationData":[OSD([sQuery(id+"F13.wireOp",EDGE,"E27.left")])],"isStart":true})});
            var Q85;
            Q85=makeQuery(id+"F14.boolean.opBoolean","COPY",EDGE,{"derivedFrom":makeQuery(id+"F14.opExtrude","CAP_EDGE",EDGE,{"disambiguationData":[OSD([sQuery(id+"F13.wireOp",EDGE,"E28.left")])],"isStart":true})});
            var Q86;
            Q86=makeQuery(id+"F14.boolean.opBoolean","COPY",EDGE,{"derivedFrom":makeQuery(id+"F14.opExtrude","CAP_EDGE",EDGE,{"disambiguationData":[OSD([sQuery(id+"F13.wireOp",EDGE,"E28.bottom")])],"isStart":true})});
            var Q87;
            Q87=makeQuery(id+"F14.boolean.opBoolean","COPY",EDGE,{"derivedFrom":makeQuery(id+"F14.opExtrude","CAP_EDGE",EDGE,{"disambiguationData":[OSD([sQuery(id+"F13.wireOp",EDGE,"E28.top")])],"isStart":true})});
            var Q88;
            Q88=makeQuery(id+"F14.boolean.opBoolean","COPY",EDGE,{"derivedFrom":makeQuery(id+"F14.opExtrude","CAP_EDGE",EDGE,{"disambiguationData":[OSD([sQuery(id+"F13.wireOp",EDGE,"E28.right")])],"isStart":true})});
            var Q89;
            Q89=makeQuery(id+"F14.boolean.opBoolean","COPY",EDGE,{"derivedFrom":makeQuery(id+"F14.opExtrude","CAP_EDGE",EDGE,{"disambiguationData":[OSD([sQuery(id+"F13.wireOp",EDGE,"E29.top")])],"isStart":true})});
            var Q90;
            Q90=makeQuery(id+"F14.boolean.opBoolean","COPY",EDGE,{"derivedFrom":makeQuery(id+"F14.opExtrude","CAP_EDGE",EDGE,{"disambiguationData":[OSD([sQuery(id+"F13.wireOp",EDGE,"E29.right")])],"isStart":true})});
            var Q91;
            Q91=makeQuery(id+"F14.boolean.opBoolean","COPY",EDGE,{"derivedFrom":makeQuery(id+"F14.opExtrude","CAP_EDGE",EDGE,{"disambiguationData":[OSD([sQuery(id+"F13.wireOp",EDGE,"E29.bottom")])],"isStart":true})});
            var Q92;
            Q92=makeQuery(id+"F14.boolean.opBoolean","COPY",EDGE,{"derivedFrom":makeQuery(id+"F14.opExtrude","CAP_EDGE",EDGE,{"disambiguationData":[OSD([sQuery(id+"F13.wireOp",EDGE,"E29.left")])],"isStart":true})});
            var Q93;
            Q93=makeQuery(id+"F14.boolean.opBoolean","COPY",EDGE,{"derivedFrom":makeQuery(id+"F14.opExtrude","CAP_EDGE",EDGE,{"disambiguationData":[OSD([sQuery(id+"F13.wireOp",EDGE,"E30.top")])],"isStart":true})});
            var Q94;
            Q94=makeQuery(id+"F14.boolean.opBoolean","INTERSECT",EDGE,{"derivedFrom":[makeQuery(id+"F1.opExtrude","SWEPT_FACE",FACE,{"disambiguationData":[OSD([sQuery(id+"F0.wireOp",EDGE,"E0.right")])]}),makeQuery(id+"F14.opExtrude","SWEPT_FACE",FACE,{"disambiguationData":[OSD([sQuery(id+"F13.wireOp",EDGE,"E30.bottom")])]})]});
            var Q95;
            Q95=makeQuery(id+"F14.boolean.opBoolean","COPY",EDGE,{"derivedFrom":makeQuery(id+"F14.opExtrude","CAP_EDGE",EDGE,{"disambiguationData":[OSD([sQuery(id+"F13.wireOp",EDGE,"E30.right")])],"isStart":true})});
            var Q96;
            Q96=makeQuery(id+"F14.boolean.opBoolean","COPY",EDGE,{"derivedFrom":makeQuery(id+"F14.opExtrude","CAP_EDGE",EDGE,{"disambiguationData":[OSD([sQuery(id+"F13.wireOp",EDGE,"E30.bottom")])],"isStart":true})});
            var Q97;
            Q97=makeQuery(id+"F14.boolean.opBoolean","COPY",EDGE,{"derivedFrom":makeQuery(id+"F14.opExtrude","CAP_EDGE",EDGE,{"disambiguationData":[OSD([sQuery(id+"F13.wireOp",EDGE,"E30.left")])],"isStart":true})});
            fillet(context, id + "F15", {"entities" : qUnion([Q0, Q1, Q2, Q3, Q4, Q5, Q6, Q7, Q8, Q9, Q10, Q11, Q12, Q13, Q14, Q15, Q16, Q17, Q18, Q19, Q20, Q21, Q22, Q23, Q24, Q25, Q26, Q27, Q28, Q29, Q30, Q31, Q32, Q33, Q34, Q35, Q36, Q37, Q38, Q39, Q40, Q41, Q42, Q43, Q44, Q45, Q46, Q47, Q48, Q49, Q50, Q51, Q52, Q53, Q54, Q55, Q56, Q57, Q58, Q59, Q60, Q61, Q62, Q63, Q64, Q65, Q66, Q67, Q68, Q69, Q70, Q71, Q72, Q73, Q74, Q75, Q76, Q77, Q78, Q79, Q80, Q81, Q82, Q83, Q84, Q85, Q86, Q87, Q88, Q89, Q90, Q91, Q92, Q93, Q94, Q95, Q96, Q97]), "radius" : .5 * mm, "tangentPropagation" : true, "allowEdgeOverflow" : false});
        }
        {
            var Q0;
            Q0=makeQuery(id+"F1.opExtrude","SWEPT_FACE",FACE,{"disambiguationData":[OSD([sQuery(id+"F0.wireOp",EDGE,"E1.right")])]});
            var sketch = newSketch(context, id + "F16", { "sketchPlane" : qUnion([Q0])});
            skText(sketch, "E31", { "text": "idk", "fontName": "OpenSans-Bold.ttf"});
            const initialGuessF16  = {"E31": [-0.00696, -0.03927, 1, 0, 0.00675]};
            skSetInitialGuess(sketch, initialGuessF16);
            skSolve(sketch);
        }
        {
            var Q0;
            Q0 = qSketchRegion(id + "F16", true);
            extrude(context, id + "F17", {"entities" : qUnion([Q0]), "operationType" : NewBodyOperationType.REMOVE, "oppositeDirection" : true, "depth" : .75 * mm, "offsetDistance" : 25 * mm});
        }
    });
